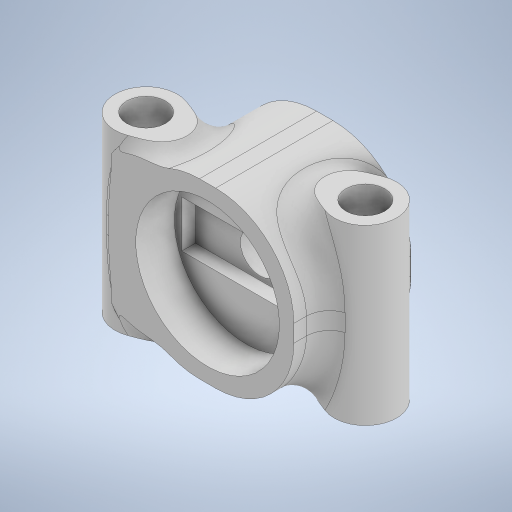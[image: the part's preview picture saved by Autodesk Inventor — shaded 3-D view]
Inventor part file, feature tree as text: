
AUTODESK INVENTOR PART (.ipt)
format: ipt  version: 2023 (Build 270158000, 158)  size: 505,344 bytes
history: native  units: in
note: dims shown in document units (in); Inventor stores cm internally (conversion verified against a paired STEP export)
features: other x4, projected_geometry x4, extrude x3, sketch x3
ambient origin geometry x8: Origin, YZ Plane, XZ Plane, XY Plane, X Axis, Y Axis, Z Axis, Center Point
bodies: Solid1 (feature_tree)
feature tree (14):
  other  "vtx antanna pre assem 1.iam"
  other  "SMA whip end.ipt:1"
  other  "4700uF cap holder.ipt:1"
  other  "4700uF cap.ipt:1"
  extrude  "Extrusion1"  Depth=0.3937in TaperAngle=0.0deg
  extrude  "Extrusion2"  Depth=0.3937in TaperAngle=0.0deg
  extrude  "Extrusion3"  [1 undecoded]
  sketch  "Sketch1"  dims[d0=0.3937in d1=0.8661in d2=0.0in]
  projected_geometry  "Projected Loop1"
  sketch  "Sketch2"  dims[d3=0.8661in d4=0.0in d5=0.3937in d6=0.0in]
  projected_geometry  "Projected Loop2"
  sketch  "Sketch4"
  projected_geometry  "Projected Loop4"
  projected_geometry  "Projected Loop5"
note: 1 required parameter value undecoded (feature->parameter linkage not recoverable at this tier; creation-order binding heuristic only, values carry confidence <= 0.55)
